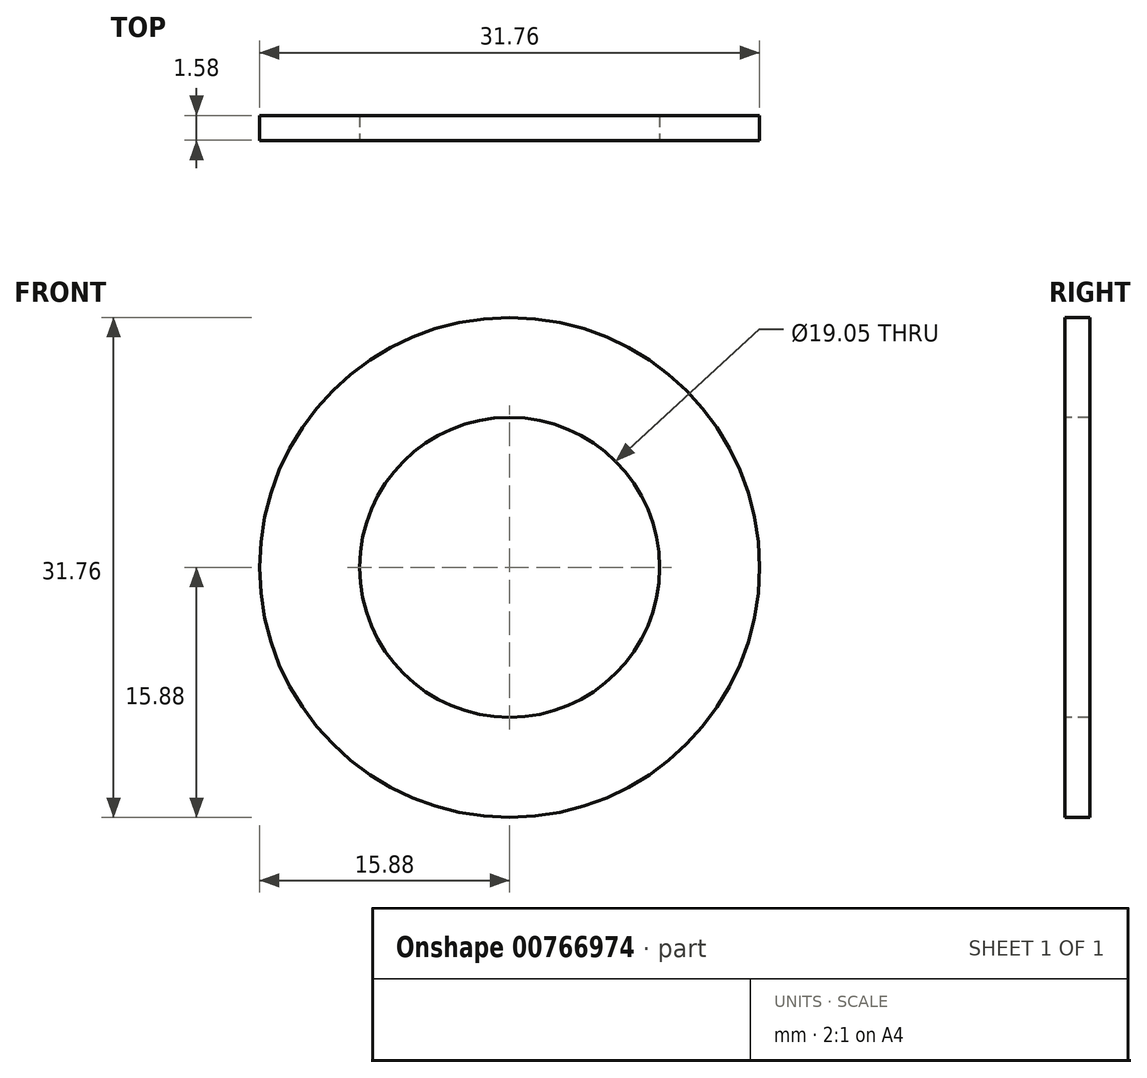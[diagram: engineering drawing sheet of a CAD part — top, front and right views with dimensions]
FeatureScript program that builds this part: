
annotation { "Feature Type Name" : "Feature", "Feature Type Description" : "" }
export const myFeature = defineFeature(function(context is Context, id is Id, definition is map)
    precondition{}
    {
        {
            var Q0;
            Q0=qCreatedBy(makeId("Front.planeOp"),FACE);
            var sketch = newSketch(context, id + "F0", { "sketchPlane" : qUnion([Q0])});
            skCircle(sketch, "E0", {"center": v(0, 0) * mm, "radius": 15.88 * mm});
            skSolve(sketch);
        }
        {
            var Q0;
            Q0 = qSketchRegion(id + "F0", true);
            extrude(context, id + "F1", {"entities" : qUnion([Q0]), "endBound" : BoundingType.SYMMETRIC, "depth" : 1.59 * mm, "offsetDistance" : 25.4 * mm});
        }
        {
            var Q0;
            Q0=makeQuery(id+"F1.opExtrude","CAP_FACE",FACE,{"disambiguationData":[OSD([sQuery(id+"F0.wireOp",EDGE,"E0")])],"isStart":false});
            var sketch = newSketch(context, id + "F2", { "sketchPlane" : qUnion([Q0])});
            skCircle(sketch, "E1", {"center": v(0, 0) * mm, "radius": 9.53 * mm});
            skSolve(sketch);
        }
        {
            var Q0;
            Q0 = qSketchRegion(id + "F2", true);
            extrude(context, id + "F3", {"entities" : qUnion([Q0]), "operationType" : NewBodyOperationType.REMOVE, "endBound" : BoundingType.THROUGH_ALL, "oppositeDirection" : true, "depth" : 25.4 * mm, "offsetDistance" : 25.4 * mm});
        }
        {
            var Q0;
            Q0 = qConstructionFilter(qBodyType(qCreatedBy(id + "F0" ,EDGE), BodyType.WIRE), ConstructionObject.NO);
            extrude(context, id + "F4", {"bodyType" : ToolBodyType.SURFACE, "operationType" : NewBodyOperationType.ADD, "surfaceEntities" : qUnion([Q0]), "oppositeDirection" : true, "depth" : 101.6 * mm, "offsetDistance" : 25.4 * mm, "hasSecondDirection" : true, "secondDirectionOppositeDirection" : false, "secondDirectionDepth" : 101.6 * mm});
        }
    });
